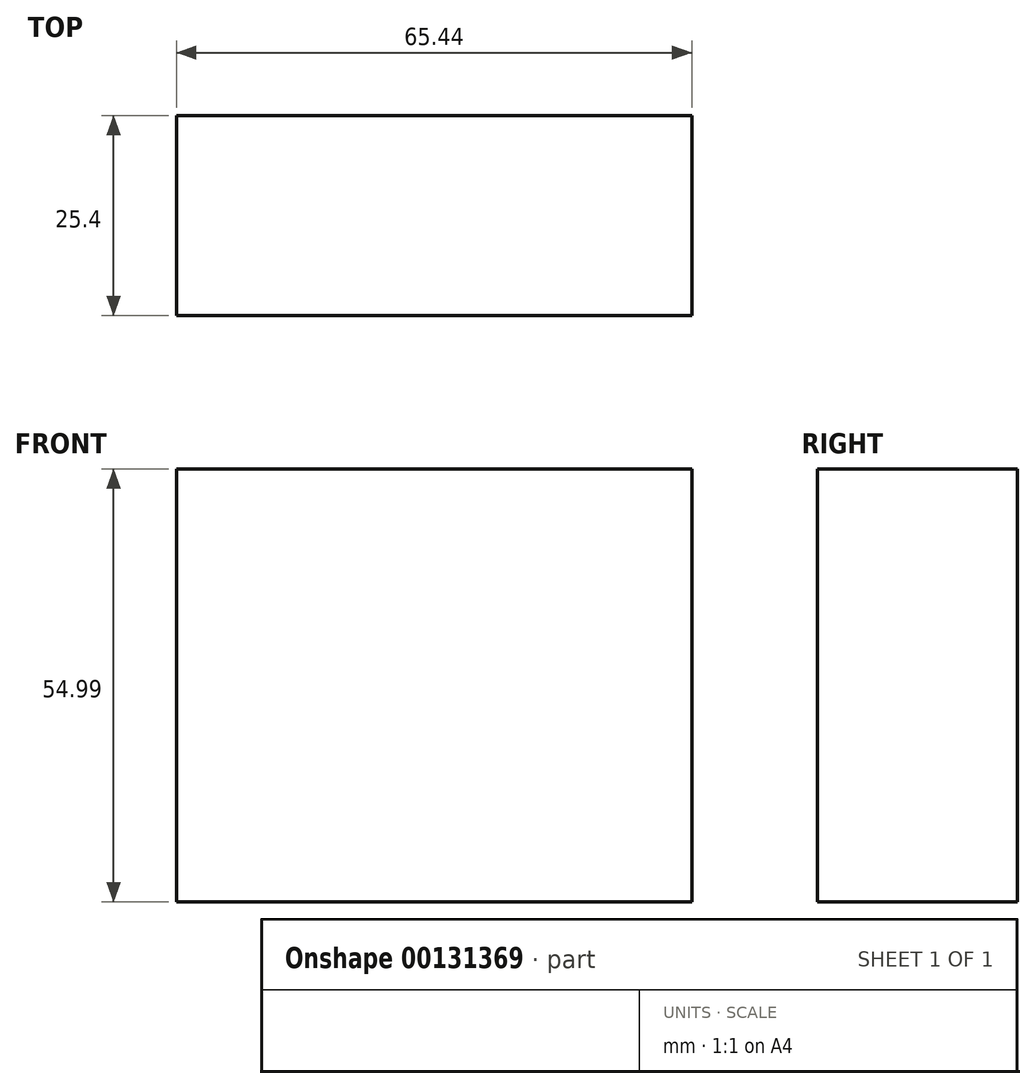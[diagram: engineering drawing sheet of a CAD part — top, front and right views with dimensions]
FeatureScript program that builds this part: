
annotation { "Feature Type Name" : "Feature", "Feature Type Description" : "" }
export const myFeature = defineFeature(function(context is Context, id is Id, definition is map)
    precondition{}
    {
        {
            var Q0;
            Q0=qCreatedBy(makeId("Front.planeOp"),FACE);
            var sketch = newSketch(context, id + "F0", { "sketchPlane" : qUnion([Q0])});
            skLineSegment(sketch, "E0.bottom", {"start": v(-32.72, -30.24) * mm, "end": v(32.72, -30.24) * mm});
            skLineSegment(sketch, "E0.top", {"start": v(-32.72, 24.75) * mm, "end": v(32.72, 24.75) * mm});
            skLineSegment(sketch, "E0.left", {"start": v(-32.72, -30.24) * mm, "end": v(-32.72, 24.75) * mm});
            skLineSegment(sketch, "E0.right", {"start": v(32.72, -30.24) * mm, "end": v(32.72, 24.75) * mm});
            skPoint(sketch, "E0.middle", {"position": v(0, -2.75) * mm});
            skSolve(sketch);
        }
        {
            var Q0;
            Q0 = qSketchRegion(id + "F0", true);
            extrude(context, id + "F1", {"entities" : qUnion([Q0]), "depth" : 25.4 * mm});
        }
    });
